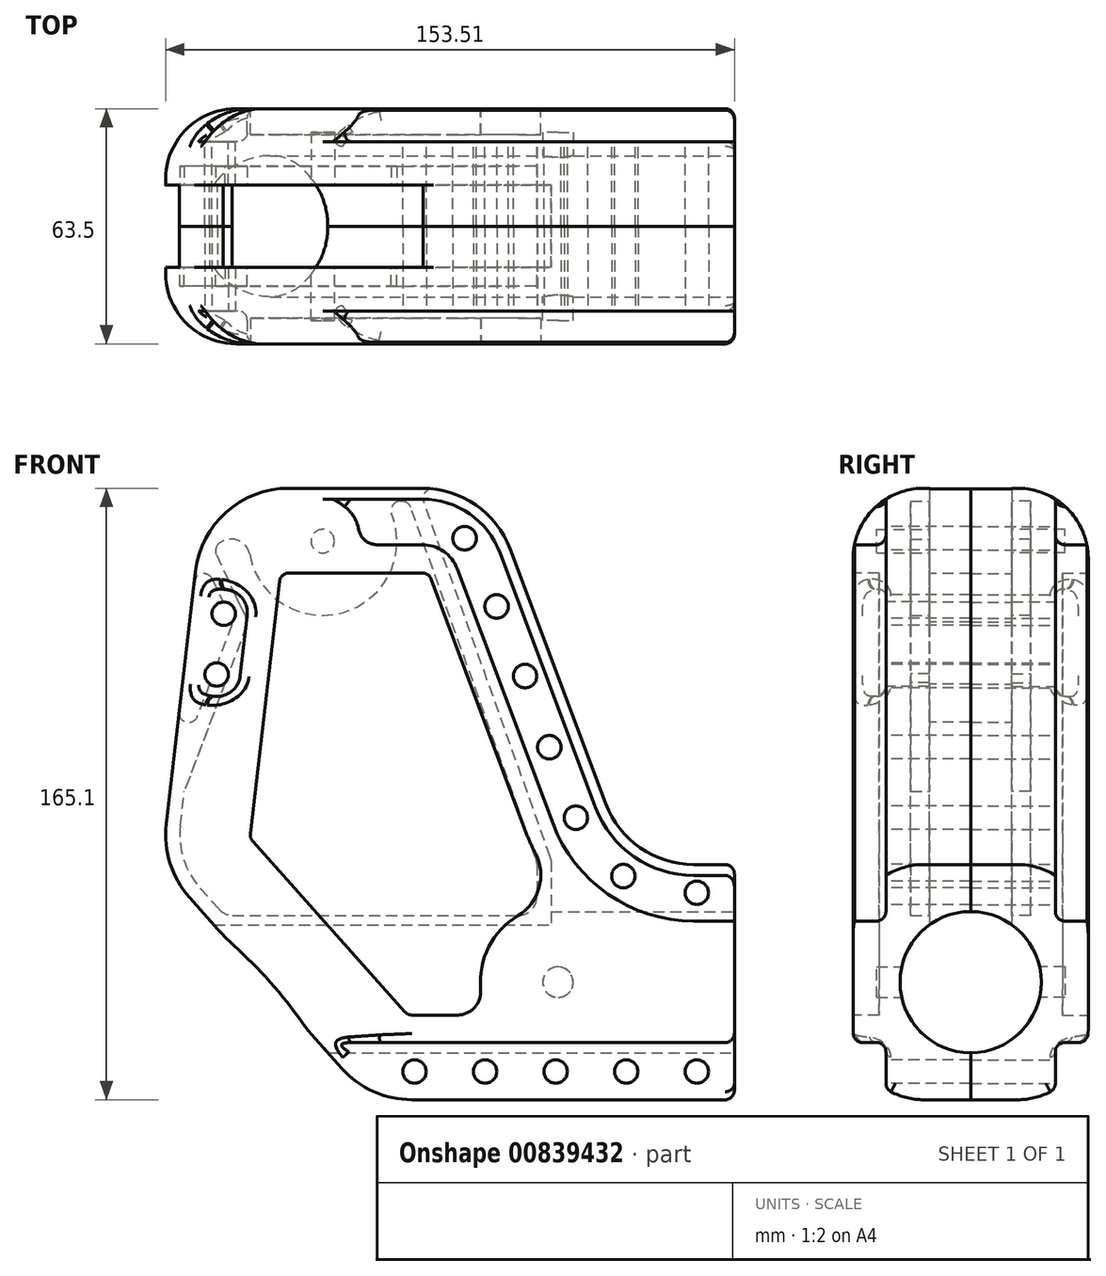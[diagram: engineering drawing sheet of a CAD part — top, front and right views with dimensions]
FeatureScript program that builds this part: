
annotation { "Feature Type Name" : "Feature", "Feature Type Description" : "" }
export const myFeature = defineFeature(function(context is Context, id is Id, definition is map)
    precondition{}
    {
        {
            var Q0;
            Q0=qCreatedBy(makeId("Right.planeOp"),FACE);
            var sketch = newSketch(context, id + "F0", { "sketchPlane" : qUnion([Q0])});
            skCircle(sketch, "E0", {"center": v(0, 0) * mm, "radius": 19.05 * mm});
            skSolve(sketch);
        }
        {
            var Q0;
            Q0=qCreatedBy(makeId("Front.planeOp"),FACE);
            var sketch = newSketch(context, id + "F1", { "sketchPlane" : qUnion([Q0])});
            skCircle(sketch, "E1", {"center": v(0, 0) * mm, "radius": 4.13 * mm});
            skLineSegment(sketch, "E2", {"start": v(0, 0) * mm, "end": v(0, 119.06) * mm, "construction": true});
            skLineSegment(sketch, "E3", {"start": v(0, 119.06) * mm, "end": v(-63.5, 119.06) * mm, "construction": true});
            skCircle(sketch, "E4", {"center": v(-63.5, 119.06) * mm, "radius": 3.18 * mm});
            skLineSegment(sketch, "E5.bottom", {"start": v(-95.25, 133.35) * mm, "end": v(-19.05, 133.35) * mm});
            skLineSegment(sketch, "E5.top", {"start": v(-76.2, -31.75) * mm, "end": v(19.05, -31.75) * mm});
            skLineSegment(sketch, "E5.right", {"start": v(19.05, 31.75) * mm, "end": v(19.05, -31.75) * mm});
            skLineSegment(sketch, "E6", {"start": v(19.05, 31.75) * mm, "end": v(-19.05, 133.35) * mm});
            skPoint(sketch, "E7.orphan", {"position": v(19.05, 133.35) * mm});
            skLineSegment(sketch, "E8", {"start": v(-76.2, -31.75) * mm, "end": v(-114.3, -31.75) * mm});
            skLineSegment(sketch, "E9", {"start": v(-114.3, -31.75) * mm, "end": v(-95.25, 133.35) * mm});
            skLineSegment(sketch, "E10", {"start": v(19.05, 31.75) * mm, "end": v(47.62, 31.75) * mm});
            skLineSegment(sketch, "E11", {"start": v(47.62, 31.75) * mm, "end": v(47.63, -31.75) * mm});
            skLineSegment(sketch, "E12", {"start": v(47.63, -31.75) * mm, "end": v(19.05, -31.75) * mm});
            skLineSegment(sketch, "E13", {"start": v(20.69, 0) * mm, "end": v(20.69, 19.05) * mm, "construction": true});
            skLineSegment(sketch, "E14", {"start": v(20.69, 19.05) * mm, "end": v(20.69, 31.75) * mm, "construction": true});
            skSolve(sketch);
        }
        {
            var Q0;
            Q0 = qSketchRegion(id + "F1", true);
            var Q1;
            Q1=makeQuery(id+"F1.imprint","IMPRINT",FACE,{"disambiguationData":[TD([[makeQuery(id+"F1.imprint","IMPRINT",EDGE,{"derivedFrom":sQuery(id+"F1.wireOp",EDGE,"E1")}),1.0]])]});
            var Q2;
            Q2=makeQuery(id+"F1.imprint","IMPRINT",FACE,{"disambiguationData":[TD([[makeQuery(id+"F1.imprint","IMPRINT",EDGE,{"derivedFrom":sQuery(id+"F1.wireOp",EDGE,"E4")}),1.0]])]});
            extrude(context, id + "F2", {"entities" : qUnion([Q0, Q1, Q2]), "depth" : 63.5 * mm, "offsetDistance" : 25.4 * mm, "symmetric" : true});
        }
        {
            var Q0;
            Q0=makeQuery(id+"F1.imprint","IMPRINT",FACE,{"disambiguationData":[TD([[makeQuery(id+"F1.imprint","IMPRINT",EDGE,{"derivedFrom":sQuery(id+"F1.wireOp",EDGE,"E1")}),1.0]])]});
            extrude(context, id + "F3", {"entities" : qUnion([Q0]), "operationType" : NewBodyOperationType.REMOVE, "depth" : 50.8 * mm, "offsetDistance" : 25.4 * mm, "symmetric" : true});
        }
        {
            var Q0;
            Q0 = qSketchRegion(id + "F0", true);
            extrude(context, id + "F4", {"entities" : qUnion([Q0]), "operationType" : NewBodyOperationType.REMOVE, "endBound" : BoundingType.THROUGH_ALL, "oppositeDirection" : true, "depth" : 25.4 * mm, "offsetDistance" : 25.4 * mm, "hasSecondDirection" : true, "secondDirectionBound" : BoundingType.THROUGH_ALL, "secondDirectionOppositeDirection" : false, "secondDirectionDepth" : 25.4 * mm});
        }
        {
            var Q0;
            Q0=qCreatedBy(makeId("Front.planeOp"),FACE);
            var sketch = newSketch(context, id + "F5", { "sketchPlane" : qUnion([Q0])});
            skLineSegment(sketch, "E15", {"start": v(-1.9, 33.34) * mm, "end": v(-38.1, 134.94) * mm});
            skLineSegment(sketch, "E16", {"start": v(-38.1, 134.94) * mm, "end": v(-105.57, 134.94) * mm});
            skLineSegment(sketch, "E17", {"start": v(-139.7, 33.34) * mm, "end": v(-1.9, 33.34) * mm});
            skLineSegment(sketch, "E18", {"start": v(-1.9, 33.34) * mm, "end": v(-1.9, 0) * mm});
            skLineSegment(sketch, "E19", {"start": v(-1.9, 0) * mm, "end": v(-139.7, 0) * mm});
            skLineSegment(sketch, "E20", {"start": v(-139.7, 0) * mm, "end": v(-139.7, 33.34) * mm});
            skLineSegment(sketch, "E21", {"start": v(-105.57, 134.94) * mm, "end": v(-87.82, 97.04) * mm});
            skLineSegment(sketch, "E22", {"start": v(-87.82, 97.04) * mm, "end": v(-111.76, 33.34) * mm});
            skPoint(sketch, "E23.start.orphan", {"position": v(-139.7, 134.94) * mm});
            skSolve(sketch);
        }
        {
            var Q0;
            Q0 = qSketchRegion(id + "F5", true);
            extrude(context, id + "F6", {"entities" : qUnion([Q0]), "operationType" : NewBodyOperationType.REMOVE, "depth" : 22.22 * mm, "offsetDistance" : 25.4 * mm, "symmetric" : true});
        }
        {
            var Q0;
            Q0=makeQuery(id+"F2.opExtrude","SWEPT_EDGE",EDGE,{"disambiguationData":[OSD([sQuery(id+"F1.wireOp",EDGE,"E8"),sQuery(id+"F1.wireOp",EDGE,"E9")])]});
            chamfer(context, id + "F7", {"entities" : qUnion([Q0]), "width" : 63.5 * mm, "tangentPropagation" : true});
        }
        {
            var Q0;
            Q0=makeQuery(id+"F2.opExtrude","SWEPT_EDGE",EDGE,{"disambiguationData":[OSD([sQuery(id+"F1.wireOp",EDGE,"E5.top"),sQuery(id+"F1.wireOp",EDGE,"E5.right")])]});
            var Q1;
            Q1=makeQuery(id+"F2.opExtrude","SWEPT_EDGE",EDGE,{"disambiguationData":[OSD([sQuery(id+"F1.wireOp",EDGE,"E5.bottom"),sQuery(id+"F1.wireOp",EDGE,"E6")])]});
            var Q2;
            {var subQ0=sQuery(id+"F1.wireOp",EDGE,"E5.bottom");var subQ1=sQuery(id+"F1.wireOp",EDGE,"E9");Q2=makeQuery(id+"F6.boolean.opBoolean","SPLIT",EDGE,{"disambiguationData":[TD([makeQuery(id+"F2.opExtrude","CAP_FACE",FACE,{"disambiguationData":[OSD([subQ0,sQuery(id+"F1.wireOp",EDGE,"E5.top"),sQuery(id+"F1.wireOp",EDGE,"E5.right"),sQuery(id+"F1.wireOp",EDGE,"E6"),sQuery(id+"F1.wireOp",EDGE,"E8"),subQ1])],"isStart":false})])],"derivedFrom":makeQuery(id+"F2.opExtrude","SWEPT_EDGE",EDGE,{"disambiguationData":[OSD([subQ0,subQ1])]})});}
            var Q3;
            {var subQ0=sQuery(id+"F1.wireOp",EDGE,"E5.bottom");var subQ1=sQuery(id+"F1.wireOp",EDGE,"E9");Q3=makeQuery(id+"F6.boolean.opBoolean","SPLIT",EDGE,{"disambiguationData":[TD([makeQuery(id+"F2.opExtrude","CAP_FACE",FACE,{"disambiguationData":[OSD([subQ0,sQuery(id+"F1.wireOp",EDGE,"E5.top"),sQuery(id+"F1.wireOp",EDGE,"E5.right"),sQuery(id+"F1.wireOp",EDGE,"E6"),sQuery(id+"F1.wireOp",EDGE,"E8"),subQ1])],"isStart":true})])],"derivedFrom":makeQuery(id+"F2.opExtrude","SWEPT_EDGE",EDGE,{"disambiguationData":[OSD([subQ0,subQ1])]})});}
            var Q4;
            {var subQ0=sQuery(id+"F1.wireOp",EDGE,"E9");Q4=makeQuery(id+"F7.opChamfer","BLEND_EDGE",EDGE,{"disambiguationData":[OD(1.0)],"blendedFrom":[makeQuery(id+"F2.opExtrude","SWEPT_EDGE",EDGE,{"disambiguationData":[OSD([sQuery(id+"F1.wireOp",EDGE,"E8"),subQ0])]}),makeQuery(id+"F2.opExtrude","SWEPT_FACE",FACE,{"disambiguationData":[OSD([subQ0])]})],"blendedInto":[makeQuery(id+"F2.opExtrude","SWEPT_FACE",FACE,{"disambiguationData":[OSD([subQ0])]})]});}
            var Q5;
            {var subQ0=sQuery(id+"F1.wireOp",EDGE,"E9");Q5=makeQuery(id+"F7.opChamfer","BLEND_EDGE",EDGE,{"disambiguationData":[OD(0.0)],"blendedFrom":[makeQuery(id+"F2.opExtrude","SWEPT_EDGE",EDGE,{"disambiguationData":[OSD([sQuery(id+"F1.wireOp",EDGE,"E8"),subQ0])]}),makeQuery(id+"F2.opExtrude","SWEPT_FACE",FACE,{"disambiguationData":[OSD([subQ0])]})],"blendedInto":[makeQuery(id+"F2.opExtrude","SWEPT_FACE",FACE,{"disambiguationData":[OSD([subQ0])]})]});}
            var Q6;
            {var subQ0=sQuery(id+"F1.wireOp",EDGE,"E8");Q6=makeQuery(id+"F7.opChamfer","BLEND_EDGE",EDGE,{"blendedFrom":[makeQuery(id+"F2.opExtrude","SWEPT_EDGE",EDGE,{"disambiguationData":[OSD([subQ0,sQuery(id+"F1.wireOp",EDGE,"E9")])]}),makeQuery(id+"F2.opExtrude","SWEPT_FACE",FACE,{"disambiguationData":[OSD([sQuery(id+"F1.wireOp",EDGE,"E5.top"),subQ0])]})],"blendedInto":[makeQuery(id+"F2.opExtrude","SWEPT_FACE",FACE,{"disambiguationData":[OSD([sQuery(id+"F1.wireOp",EDGE,"E5.top"),subQ0])]})]});}
            var Q7;
            Q7=makeQuery(id+"F2.opExtrude","SWEPT_EDGE",EDGE,{"disambiguationData":[OSD([sQuery(id+"F1.wireOp",EDGE,"E5.right"),sQuery(id+"F1.wireOp",EDGE,"E6")])]});
            fillet(context, id + "F8", {"entities" : qUnion([Q0, Q1, Q2, Q3, Q4, Q5, Q6, Q7]), "tangentPropagation" : true, "radius" : 25.4 * mm, "defaultsChanged" : false, "vertexSettings" : [], "allowEdgeOverflow" : false});
        }
        {
            var Q0;
            Q0=makeQuery(id+"F1.imprint","IMPRINT",FACE,{"disambiguationData":[TD([[makeQuery(id+"F1.imprint","IMPRINT",EDGE,{"derivedFrom":sQuery(id+"F1.wireOp",EDGE,"E4")}),1.0]])]});
            extrude(context, id + "F9", {"entities" : qUnion([Q0]), "operationType" : NewBodyOperationType.REMOVE, "depth" : 50.8 * mm, "offsetDistance" : 25.4 * mm, "symmetric" : true});
        }
        {
            var Q0;
            Q0=makeQuery(id+"F2.opExtrude","CAP_FACE",FACE,{"disambiguationData":[OSD([sQuery(id+"F1.wireOp",EDGE,"E5.bottom"),sQuery(id+"F1.wireOp",EDGE,"E5.top"),sQuery(id+"F1.wireOp",EDGE,"E5.right"),sQuery(id+"F1.wireOp",EDGE,"E6"),sQuery(id+"F1.wireOp",EDGE,"E8"),sQuery(id+"F1.wireOp",EDGE,"E9")])],"isStart":false});
            var sketch = newSketch(context, id + "F10", { "sketchPlane" : qUnion([Q0])});
            skLineSegment(sketch, "E24", {"start": v(0, 0) * mm, "end": v(108.17, 0) * mm, "construction": true});
            skCircle(sketch, "E25", {"center": v(37.47, -24.13) * mm, "radius": 3.17 * mm});
            skCircle(sketch, "E26.MirrorC", {"center": v(37.47, 24.13) * mm, "radius": 3.17 * mm});
            skCircle(sketch, "E27.1.0.0", {"center": v(18.42, -24.13) * mm, "radius": 3.17 * mm});
            skCircle(sketch, "E27.2.0.0", {"center": v(-0.63, -24.13) * mm, "radius": 3.17 * mm});
            skCircle(sketch, "E27.3.0.0", {"center": v(-19.68, -24.13) * mm, "radius": 3.17 * mm});
            skCircle(sketch, "E27.4.0.0", {"center": v(-38.73, -24.13) * mm, "radius": 3.17 * mm});
            skLineSegment(sketch, "E27.direction1", {"start": v(37.47, -24.13) * mm, "end": v(18.42, -24.13) * mm, "construction": true});
            skCircle(sketch, "E28", {"center": v(17.65, 28.61) * mm, "radius": 3.18 * mm});
            skCircle(sketch, "E29", {"center": v(4.83, 44.38) * mm, "radius": 3.18 * mm});
            skCircle(sketch, "E30", {"center": v(-2.31, 63.4) * mm, "radius": 3.18 * mm});
            skCircle(sketch, "E31", {"center": v(-8.89, 82.63) * mm, "radius": 3.18 * mm});
            skCircle(sketch, "E32", {"center": v(-16.58, 101.44) * mm, "radius": 3.18 * mm});
            skCircle(sketch, "E33", {"center": v(-25.2, 119.84) * mm, "radius": 3.17 * mm});
            skCircle(sketch, "E34", {"center": v(-90.21, 99.46) * mm, "radius": 3.18 * mm});
            skCircle(sketch, "E35", {"center": v(-92.1, 83.06) * mm, "radius": 3.18 * mm});
            skSolve(sketch);
        }
        {
            var Q0;
            Q0 = qSketchRegion(id + "F10", true);
            extrude(context, id + "F11", {"entities" : qUnion([Q0]), "operationType" : NewBodyOperationType.REMOVE, "endBound" : BoundingType.THROUGH_ALL, "oppositeDirection" : true, "depth" : 25.4 * mm, "offsetDistance" : 25.4 * mm});
        }
        {
            var Q0;
            Q0=makeQuery(id+"F2.opExtrude","CAP_EDGE",EDGE,{"disambiguationData":[OSD([sQuery(id+"F1.wireOp",EDGE,"E6")])],"isStart":false});
            var Q1;
            Q1=makeQuery(id+"F2.opExtrude","CAP_EDGE",EDGE,{"disambiguationData":[OSD([sQuery(id+"F1.wireOp",EDGE,"E6")])],"isStart":true});
            fillet(context, id + "F12", {"entities" : qUnion([Q0, Q1]), "tangentPropagation" : true, "radius" : 19.05 * mm, "defaultsChanged" : false, "vertexSettings" : [], "allowEdgeOverflow" : false});
        }
        {
            var Q0;
            Q0=makeQuery(id+"F8.opFillet","BLEND_EDGE",EDGE,{"blendedFrom":[makeQuery(id+"F2.opExtrude","SWEPT_EDGE",EDGE,{"disambiguationData":[OSD([sQuery(id+"F1.wireOp",EDGE,"E5.bottom"),sQuery(id+"F1.wireOp",EDGE,"E6")])]}),makeQuery(id+"F6.boolean.opBoolean","COPY",FACE,{"derivedFrom":makeQuery(id+"F6.opExtrude","SWEPT_FACE",FACE,{"disambiguationData":[OSD([sQuery(id+"F5.wireOp",EDGE,"E15")])]})})],"blendedInto":[makeQuery(id+"F6.boolean.opBoolean","COPY",FACE,{"derivedFrom":makeQuery(id+"F6.opExtrude","SWEPT_FACE",FACE,{"disambiguationData":[OSD([sQuery(id+"F5.wireOp",EDGE,"E15")])]})})]});
            var Q1;
            Q1=makeQuery(id+"F6.boolean.opBoolean","COPY",EDGE,{"derivedFrom":makeQuery(id+"F6.opExtrude","SWEPT_EDGE",EDGE,{"disambiguationData":[OSD([sQuery(id+"F5.wireOp",EDGE,"E15"),sQuery(id+"F5.wireOp",EDGE,"E17"),sQuery(id+"F5.wireOp",EDGE,"E18")])]})});
            fillet(context, id + "F13", {"entities" : qUnion([Q0, Q1]), "tangentPropagation" : true, "radius" : 3.17 * mm, "defaultsChanged" : false, "vertexSettings" : [], "allowEdgeOverflow" : false});
        }
        {
            var Q0;
            Q0=makeQuery(id+"F2.opExtrude","CAP_FACE",FACE,{"disambiguationData":[OSD([sQuery(id+"F1.wireOp",EDGE,"E5.bottom"),sQuery(id+"F1.wireOp",EDGE,"E5.top"),sQuery(id+"F1.wireOp",EDGE,"E5.right"),sQuery(id+"F1.wireOp",EDGE,"E6"),sQuery(id+"F1.wireOp",EDGE,"E8"),sQuery(id+"F1.wireOp",EDGE,"E9")])],"isStart":false});
            var sketch = newSketch(context, id + "F14", { "sketchPlane" : qUnion([Q0])});
            skLineSegment(sketch, "E36.0", {"start": v(-39.41, -8.89) * mm, "end": v(-27.19, -8.89) * mm});
            skLineSegment(sketch, "E36.1", {"start": v(-82.38, 38.04) * mm, "end": v(-41.31, -8.04) * mm});
            skLineSegment(sketch, "E36.2", {"start": v(-75.14, 108.24) * mm, "end": v(-83, 40.02) * mm});
            skLineSegment(sketch, "E36.5", {"start": v(-8.54, 40.2) * mm, "end": v(-34.27, 108.84) * mm});
            skLineSegment(sketch, "E36.6", {"start": v(-36.65, 110.5) * mm, "end": v(-72.61, 110.5) * mm});
            skArc(sketch, "E37.trimOffspring", {"start": v(-10.8, 17.96) * mm, "mid": v(-18.7, 9.46) * mm, "end": v(-20.86, -1.95) * mm});
            skArc(sketch, "E38.trimOffspring", {"start": v(-6.1, 34.74) * mm, "mid": v(-7.4, 37.44) * mm, "end": v(-8.54, 40.2) * mm});
            skPoint(sketch, "E39.visualSharp", {"position": v(-34.9, 110.5) * mm});
            skArc(sketch, "E39.filletArc", {"start": v(-34.27, 108.84) * mm, "mid": v(-35.2, 110.04) * mm, "end": v(-36.65, 110.5) * mm});
            skPoint(sketch, "E40.visualSharp", {"position": v(-74.88, 110.5) * mm});
            skArc(sketch, "E40.filletArc", {"start": v(-72.61, 110.5) * mm, "mid": v(-74.3, 109.85) * mm, "end": v(-75.14, 108.24) * mm});
            skPoint(sketch, "E41.visualSharp", {"position": v(-83.14, 38.9) * mm});
            skArc(sketch, "E41.filletArc", {"start": v(-83, 40.02) * mm, "mid": v(-82.9, 38.96) * mm, "end": v(-82.38, 38.04) * mm});
            skPoint(sketch, "E42.visualSharp", {"position": v(-40.55, -8.89) * mm});
            skArc(sketch, "E42.filletArc", {"start": v(-41.31, -8.04) * mm, "mid": v(-40.45, -8.67) * mm, "end": v(-39.41, -8.89) * mm});
            skPoint(sketch, "E43.visualSharp", {"position": v(-18.98, -8.89) * mm});
            skArc(sketch, "E43.filletArc", {"start": v(-27.19, -8.89) * mm, "mid": v(-22.5, -6.82) * mm, "end": v(-20.86, -1.95) * mm});
            skPoint(sketch, "E44.visualSharp", {"position": v(5.63, 20.19) * mm});
            skArc(sketch, "E44.filletArc", {"start": v(-10.8, 17.96) * mm, "mid": v(-5.1, 25.42) * mm, "end": v(-6.1, 34.74) * mm});
            skPoint(sketch, "E45.visualSharp", {"position": v(16, 13.53) * mm});
            skPoint(sketch, "E46.visualSharp", {"position": v(18.98, -8.89) * mm});
            skArc(sketch, "E47.0", {"start": v(-27.14, 111.52) * mm, "mid": v(-30.87, 116.3) * mm, "end": v(-36.65, 118.11) * mm});
            skLineSegment(sketch, "E47.1", {"start": v(-1.4, 42.88) * mm, "end": v(-27.14, 111.52) * mm});
            skArc(sketch, "E47.2", {"start": v(36.65, 16.51) * mm, "mid": v(13.5, 23.75) * mm, "end": v(-1.4, 42.88) * mm});
            skLineSegment(sketch, "E47.3", {"start": v(47.63, 16.51) * mm, "end": v(36.65, 16.51) * mm});
            skLineSegment(sketch, "E48", {"start": v(-31.55, 138.14) * mm, "end": v(24.8, 112.47) * mm});
            skLineSegment(sketch, "E49", {"start": v(24.8, 112.47) * mm, "end": v(58.9, 66.28) * mm});
            skLineSegment(sketch, "E50", {"start": v(58.9, 66.28) * mm, "end": v(47.62, 16.5) * mm});
            skLineSegment(sketch, "E51.1", {"start": v(-36.65, 118.11) * mm, "end": v(-48.8, 118.11) * mm});
            skArc(sketch, "E52", {"start": v(-53.8, 122.3) * mm, "mid": v(-57.14, 128.06) * mm, "end": v(-63.41, 130.34) * mm});
            skPoint(sketch, "E53.visualSharp", {"position": v(-53.96, 118.11) * mm});
            skArc(sketch, "E53.filletArc", {"start": v(-53.8, 122.3) * mm, "mid": v(-52.06, 119.3) * mm, "end": v(-48.8, 118.11) * mm});
            skLineSegment(sketch, "E54", {"start": v(51.1, -16.3) * mm, "end": v(-82.45, -16.3) * mm});
            skLineSegment(sketch, "E55", {"start": v(-82.45, -16.3) * mm, "end": v(-82.45, -34.82) * mm});
            skLineSegment(sketch, "E56", {"start": v(-82.45, -34.82) * mm, "end": v(52.34, -34.82) * mm});
            skLineSegment(sketch, "E57", {"start": v(52.34, -34.82) * mm, "end": v(51.1, -16.3) * mm});
            skLineSegment(sketch, "E58", {"start": v(-63.41, 130.34) * mm, "end": v(-63.41, 138.14) * mm});
            skLineSegment(sketch, "E59", {"start": v(-63.41, 138.14) * mm, "end": v(-31.55, 138.14) * mm});
            skLineSegment(sketch, "E60.0", {"start": v(-83.88, 98.94) * mm, "end": v(-85.75, 82.73) * mm});
            skLineSegment(sketch, "E61", {"start": v(-89.46, 105.98) * mm, "end": v(-102.52, 107.49) * mm});
            skLineSegment(sketch, "E62", {"start": v(-102.52, 107.49) * mm, "end": v(-105.85, 78.66) * mm});
            skLineSegment(sketch, "E63", {"start": v(-105.85, 78.66) * mm, "end": v(-92.79, 77.15) * mm});
            skPoint(sketch, "E64.visualSharp", {"position": v(-83.15, 105.25) * mm});
            skArc(sketch, "E64.filletArc", {"start": v(-83.88, 98.94) * mm, "mid": v(-85.21, 103.62) * mm, "end": v(-89.46, 105.98) * mm});
            skArc(sketch, "E65.filletArc", {"start": v(-92.79, 77.15) * mm, "mid": v(-88.11, 78.48) * mm, "end": v(-85.75, 82.73) * mm});
            skSolve(sketch);
        }
        {
            var Q0;
            {var subQ1=sQuery(id+"F14.wireOp",EDGE,"E36.3");Q0=makeQuery(id+"F14.imprint","IMPRINT",FACE,{"disambiguationData":[TD([[makeQuery(id+"F14.imprint","IMPRINT",EDGE,{"derivedFrom":subQ1}),1.0]])]});}
            var Q1;
            Q1=makeQuery(id+"F14.imprint","IMPRINT",FACE,{"disambiguationData":[TD([[makeQuery(id+"F14.imprint","IMPRINT",EDGE,{"derivedFrom":sQuery(id+"F14.wireOp",EDGE,"E36.0")}),1.0]])]});
            extrude(context, id + "F15", {"entities" : qUnion([Q0, Q1]), "operationType" : NewBodyOperationType.REMOVE, "oppositeDirection" : true, "depth" : 7 * mm, "offsetDistance" : 25.4 * mm});
        }
        {
            var Q0;
            Q0=makeQuery(id+"F12.opFillet","BLEND_EDGE",EDGE,{"blendedFrom":[makeQuery(id+"F2.opExtrude","CAP_EDGE",EDGE,{"disambiguationData":[OSD([sQuery(id+"F1.wireOp",EDGE,"E10")])],"isStart":false}),makeQuery(id+"F2.opExtrude","SWEPT_FACE",FACE,{"disambiguationData":[OSD([sQuery(id+"F1.wireOp",EDGE,"E11")])]})],"blendedInto":[makeQuery(id+"F2.opExtrude","SWEPT_FACE",FACE,{"disambiguationData":[OSD([sQuery(id+"F1.wireOp",EDGE,"E11")])]})]});
            fillet(context, id + "F16", {"entities" : qUnion([Q0]), "tangentPropagation" : true, "radius" : 2.54 * mm, "defaultsChanged" : true, "vertexSettings" : [], "allowEdgeOverflow" : false});
        }
        {
            var Q0;
            Q0=makeQuery(id+"F14.imprint","IMPRINT",FACE,{"disambiguationData":[TD([[makeQuery(id+"F14.imprint","IMPRINT",EDGE,{"derivedFrom":sQuery(id+"F14.wireOp",EDGE,"E47.0")}),-1.0]])]});
            var Q1;
            Q1=makeQuery(id+"F14.imprint","IMPRINT",FACE,{"disambiguationData":[TD([[makeQuery(id+"F14.imprint","IMPRINT",EDGE,{"derivedFrom":sQuery(id+"F14.wireOp",EDGE,"E54")}),1.0]])]});
            var Q2;
            Q2=makeQuery(id+"F14.imprint","IMPRINT",FACE,{"disambiguationData":[TD([[makeQuery(id+"F14.imprint","IMPRINT",EDGE,{"derivedFrom":sQuery(id+"F14.wireOp",EDGE,"E60.0")}),-1.0]])]});
            extrude(context, id + "F17", {"entities" : qUnion([Q0, Q1, Q2]), "operationType" : NewBodyOperationType.REMOVE, "oppositeDirection" : true, "depth" : 8.9 * mm, "offsetDistance" : 25.4 * mm});
        }
        {
            var Q0;
            Q0=makeQuery(id+"F17.boolean.opBoolean","COPY",EDGE,{"derivedFrom":makeQuery(id+"F17.opExtrude","CAP_EDGE",EDGE,{"disambiguationData":[OSD([sQuery(id+"F14.wireOp",EDGE,"E47.1")])],"isStart":false})});
            var Q1;
            Q1=makeQuery(id+"F17.boolean.opBoolean","COPY",EDGE,{"derivedFrom":makeQuery(id+"F17.opExtrude","CAP_EDGE",EDGE,{"disambiguationData":[OSD([sQuery(id+"F14.wireOp",EDGE,"E54")])],"isStart":false})});
            var Q2;
            Q2=makeQuery(id+"F17.boolean.opBoolean","COPY",EDGE,{"derivedFrom":makeQuery(id+"F17.opExtrude","CAP_EDGE",EDGE,{"disambiguationData":[OSD([sQuery(id+"F14.wireOp",EDGE,"E60.0")])],"isStart":false})});
            fillet(context, id + "F18", {"entities" : qUnion([Q0, Q1, Q2]), "tangentPropagation" : true, "radius" : 2.54 * mm, "defaultsChanged" : false, "vertexSettings" : [], "allowEdgeOverflow" : false});
        }
        {
            var Q0;
            {var subQ0=sQuery(id+"F1.wireOp",EDGE,"E12");var subQ1=sQuery(id+"F1.wireOp",EDGE,"E8");var subQ2=sQuery(id+"F1.wireOp",EDGE,"E5.top");Q0=makeQuery(id+"F17.boolean.opBoolean","INTERSECT",EDGE,{"derivedFrom":[makeQuery(id+"F12.opFillet","BLEND_FACE",FACE,{"disambiguationData":[OSD([subQ2,subQ1,subQ0]),TDD([makeQuery(id+"F2.opExtrude","CAP_EDGE",EDGE,{"disambiguationData":[OSD([subQ2,subQ1,subQ0])],"isStart":false})])]}),makeQuery(id+"F17.opExtrude","SWEPT_FACE",FACE,{"disambiguationData":[OSD([sQuery(id+"F14.wireOp",EDGE,"E54")])]})]});}
            var Q1;
            {var subQ0=sQuery(id+"F1.wireOp",EDGE,"E12");var subQ1=sQuery(id+"F1.wireOp",EDGE,"E8");var subQ2=sQuery(id+"F1.wireOp",EDGE,"E5.top");Q1=makeQuery(id+"F17.boolean.opBoolean","INTERSECT",EDGE,{"derivedFrom":[makeQuery(id+"F12.opFillet","BLEND_FACE",FACE,{"disambiguationData":[OSD([subQ2,subQ1,subQ0]),TDD([makeQuery(id+"F2.opExtrude","CAP_EDGE",EDGE,{"disambiguationData":[OSD([subQ2,subQ1,subQ0])],"isStart":false})])]}),makeQuery(id+"F17.opExtrude","CAP_FACE",FACE,{"disambiguationData":[OSD([sQuery(id+"F14.wireOp",EDGE,"E54"),sQuery(id+"F14.wireOp",EDGE,"E55"),sQuery(id+"F14.wireOp",EDGE,"E56"),sQuery(id+"F14.wireOp",EDGE,"E57")])],"isStart":false})]});}
            var Q2;
            {var subQ0=sQuery(id+"F1.wireOp",EDGE,"E12");var subQ1=sQuery(id+"F1.wireOp",EDGE,"E11");var subQ2=sQuery(id+"F1.wireOp",EDGE,"E10");var subQ3=sQuery(id+"F1.wireOp",EDGE,"E9");var subQ4=sQuery(id+"F1.wireOp",EDGE,"E8");var subQ5=sQuery(id+"F1.wireOp",EDGE,"E6");var subQ6=sQuery(id+"F1.wireOp",EDGE,"E5.top");var subQ7=sQuery(id+"F1.wireOp",EDGE,"E5.bottom");var subQ8=sQuery(id+"F1.wireOp",EDGE,"E5.right");Q2=makeQuery(id+"F17.boolean.opBoolean","INTERSECT",EDGE,{"derivedFrom":[makeQuery(id+"F12.opFillet","BLEND_FACE",FACE,{"disambiguationData":[OSD([subQ7,subQ6,subQ8,subQ5,subQ4,subQ3,subQ2,subQ1,subQ0]),TDD([makeQuery(id+"F8.opFillet","BLEND_EDGE",EDGE,{"blendedFrom":[makeQuery(id+"F2.opExtrude","SWEPT_EDGE",EDGE,{"disambiguationData":[OSD([subQ8,subQ5,subQ2])]}),makeQuery(id+"F2.opExtrude","CAP_FACE",FACE,{"disambiguationData":[OSD([subQ7,subQ6,subQ5,subQ4,subQ3,subQ2,subQ1,subQ0])],"isStart":false})],"blendedInto":[makeQuery(id+"F2.opExtrude","CAP_FACE",FACE,{"disambiguationData":[OSD([subQ7,subQ6,subQ5,subQ4,subQ3,subQ2,subQ1,subQ0])],"isStart":false})]})])]}),makeQuery(id+"F17.opExtrude","SWEPT_FACE",FACE,{"disambiguationData":[OSD([sQuery(id+"F14.wireOp",EDGE,"E47.2")])]})]});}
            var Q3;
            Q3=makeQuery(id+"F15.boolean.opBoolean","COPY",EDGE,{"derivedFrom":makeQuery(id+"F15.opExtrude","CAP_EDGE",EDGE,{"disambiguationData":[OSD([sQuery(id+"F14.wireOp",EDGE,"E36.5")])],"isStart":true})});
            var Q4;
            {var subQ0=sQuery(id+"F1.wireOp",EDGE,"E9");Q4=makeQuery(id+"F17.boolean.opBoolean","INTERSECT",EDGE,{"derivedFrom":[makeQuery(id+"F12.opFillet","BLEND_FACE",FACE,{"disambiguationData":[OSD([subQ0]),TDD([makeQuery(id+"F2.opExtrude","CAP_EDGE",EDGE,{"disambiguationData":[OSD([subQ0])],"isStart":false})])]}),makeQuery(id+"F17.opExtrude","SWEPT_FACE",FACE,{"disambiguationData":[OSD([sQuery(id+"F14.wireOp",EDGE,"E60.0")])]})]});}
            fillet(context, id + "F19", {"entities" : qUnion([Q0, Q1, Q2, Q3, Q4]), "tangentPropagation" : true, "radius" : 2.54 * mm, "defaultsChanged" : false, "vertexSettings" : [], "allowEdgeOverflow" : false});
        }
        {
            var Q0;
            Q0=qCreatedBy(makeId("Front.planeOp"),FACE);
            var sketch = newSketch(context, id + "F20", { "sketchPlane" : qUnion([Q0])});
            skLineSegment(sketch, "E66.bottom", {"start": v(-108.56, -43.65) * mm, "end": v(63.43, -43.65) * mm});
            skLineSegment(sketch, "E66.top", {"start": v(-108.56, 138.76) * mm, "end": v(63.43, 138.76) * mm});
            skLineSegment(sketch, "E66.left", {"start": v(-108.56, -43.65) * mm, "end": v(-108.56, 138.76) * mm});
            skLineSegment(sketch, "E66.right", {"start": v(63.43, -43.65) * mm, "end": v(63.43, 138.76) * mm});
            skSolve(sketch);
        }
        {
            var Q0;
            Q0 = qSketchRegion(id + "F20", true);
            extrude(context, id + "F21", {"entities" : qUnion([Q0]), "operationType" : NewBodyOperationType.REMOVE, "endBound" : BoundingType.THROUGH_ALL, "oppositeDirection" : true, "depth" : 25.4 * mm, "offsetDistance" : 25.4 * mm});
        }
        {
            var Q0;
            Q0=makeQuery(id+"F6.boolean.opBoolean","COPY",FACE,{"derivedFrom":makeQuery(id+"F6.opExtrude","CAP_FACE",FACE,{"disambiguationData":[OSD([sQuery(id+"F5.wireOp",EDGE,"E15"),sQuery(id+"F5.wireOp",EDGE,"E16"),sQuery(id+"F5.wireOp",EDGE,"E23"),sQuery(id+"F5.wireOp",EDGE,"E18"),sQuery(id+"F5.wireOp",EDGE,"E19"),sQuery(id+"F5.wireOp",EDGE,"E20")])],"isStart":false})});
            var sketch = newSketch(context, id + "F22", { "sketchPlane" : qUnion([Q0])});
            skArc(sketch, "E67", {"start": v(44.87, 126.4) * mm, "mid": v(58.01, 99.81) * mm, "end": v(83.2, 115.47) * mm});
            skArc(sketch, "E68.1", {"start": v(96.6, 25.37) * mm, "mid": v(101.07, 33.22) * mm, "end": v(101.93, 42.2) * mm});
            skLineSegment(sketch, "E68.3", {"start": v(91.56, 19.7) * mm, "end": v(96.6, 25.37) * mm});
            skLineSegment(sketch, "E68.4", {"start": v(42.51, 129.86) * mm, "end": v(42.13, 129.86) * mm});
            skLineSegment(sketch, "E68.5", {"start": v(6, 33.5) * mm, "end": v(39.74, 128.18) * mm});
            skLineSegment(sketch, "E68.6", {"start": v(5.7, 31.8) * mm, "end": v(5.7, 23.09) * mm});
            skLineSegment(sketch, "E68.7", {"start": v(87.77, 18) * mm, "end": v(10.78, 18) * mm});
            skPoint(sketch, "E69.visualSharp", {"position": v(81.3, 128.22) * mm});
            skArc(sketch, "E69.filletArc", {"start": v(91.6, 118.32) * mm, "mid": v(86.56, 119.37) * mm, "end": v(83.2, 115.47) * mm});
            skPoint(sketch, "E70.visualSharp", {"position": v(46.65, 129.86) * mm});
            skArc(sketch, "E70.filletArc", {"start": v(44.87, 126.4) * mm, "mid": v(44.61, 128.75) * mm, "end": v(42.51, 129.86) * mm});
            skPoint(sketch, "E71.visualSharp", {"position": v(40.34, 129.86) * mm});
            skArc(sketch, "E71.filletArc", {"start": v(42.13, 129.86) * mm, "mid": v(40.66, 129.4) * mm, "end": v(39.74, 128.18) * mm});
            skPoint(sketch, "E72.visualSharp", {"position": v(5.7, 32.68) * mm});
            skArc(sketch, "E72.filletArc", {"start": v(6, 33.5) * mm, "mid": v(5.77, 32.67) * mm, "end": v(5.7, 31.8) * mm});
            skPoint(sketch, "E73.visualSharp", {"position": v(5.7, 18) * mm});
            skArc(sketch, "E73.filletArc", {"start": v(5.7, 23.09) * mm, "mid": v(7.19, 19.5) * mm, "end": v(10.78, 18) * mm});
            skPoint(sketch, "E74.visualSharp", {"position": v(90.04, 18) * mm});
            skArc(sketch, "E74.filletArc", {"start": v(87.77, 18) * mm, "mid": v(89.84, 18.45) * mm, "end": v(91.56, 19.7) * mm});
            skLineSegment(sketch, "E75.0", {"start": v(101.93, 42.2) * mm, "end": v(100.86, 51.52) * mm});
            skLineSegment(sketch, "E75.1", {"start": v(84.07, 96.2) * mm, "end": v(100.86, 51.52) * mm});
            skLineSegment(sketch, "E75.2", {"start": v(92.2, 115.36) * mm, "end": v(84.14, 98.18) * mm});
            skPoint(sketch, "E76.visualSharp", {"position": v(83.7, 97.2) * mm});
            skArc(sketch, "E76.filletArc", {"start": v(84.14, 98.18) * mm, "mid": v(83.9, 97.2) * mm, "end": v(84.07, 96.2) * mm});
            skPoint(sketch, "E77.visualSharp", {"position": v(92.8, 116.67) * mm});
            skArc(sketch, "E77.filletArc", {"start": v(92.2, 115.36) * mm, "mid": v(92.38, 116.94) * mm, "end": v(91.6, 118.32) * mm});
            skSolve(sketch);
        }
        {
            var Q0;
            Q0 = qSketchRegion(id + "F22", true);
            extrude(context, id + "F23", {"entities" : qUnion([Q0]), "operationType" : NewBodyOperationType.REMOVE, "oppositeDirection" : true, "depth" : 5.08 * mm, "offsetDistance" : 25.4 * mm});
        }
        {
            var Q0;
            {var subQ0=sQuery(id+"F5.wireOp",EDGE,"E21");var subQ1=sQuery(id+"F1.wireOp",EDGE,"E5.bottom");var subQ2=sQuery(id+"F1.wireOp",EDGE,"E9");Q0=makeQuery(id+"F25.opPattern","COPY",EDGE,{"derivedFrom":makeQuery(id+"F8.opFillet","BLEND_EDGE",EDGE,{"blendedFrom":[makeQuery(id+"F6.boolean.opBoolean","SPLIT",EDGE,{"disambiguationData":[TD([makeQuery(id+"F2.opExtrude","CAP_FACE",FACE,{"disambiguationData":[OSD([subQ1,sQuery(id+"F1.wireOp",EDGE,"E5.top"),sQuery(id+"F1.wireOp",EDGE,"E6"),sQuery(id+"F1.wireOp",EDGE,"E8"),subQ2,sQuery(id+"F1.wireOp",EDGE,"E10"),sQuery(id+"F1.wireOp",EDGE,"E11"),sQuery(id+"F1.wireOp",EDGE,"E12")])],"isStart":false})])],"derivedFrom":makeQuery(id+"F2.opExtrude","SWEPT_EDGE",EDGE,{"disambiguationData":[OSD([subQ1,subQ2])]})}),makeQuery(id+"F6.boolean.opBoolean","COPY",FACE,{"derivedFrom":makeQuery(id+"F6.opExtrude","SWEPT_FACE",FACE,{"disambiguationData":[OSD([subQ0])]})})],"blendedInto":[makeQuery(id+"F6.boolean.opBoolean","COPY",FACE,{"derivedFrom":makeQuery(id+"F6.opExtrude","SWEPT_FACE",FACE,{"disambiguationData":[OSD([subQ0])]})})]}),"instanceName":"1"});}
            var Q1;
            {var subQ0=sQuery(id+"F5.wireOp",EDGE,"E21");var subQ1=sQuery(id+"F1.wireOp",EDGE,"E5.bottom");var subQ2=sQuery(id+"F1.wireOp",EDGE,"E9");Q1=makeQuery(id+"F8.opFillet","BLEND_EDGE",EDGE,{"blendedFrom":[makeQuery(id+"F6.boolean.opBoolean","SPLIT",EDGE,{"disambiguationData":[TD([makeQuery(id+"F2.opExtrude","CAP_FACE",FACE,{"disambiguationData":[OSD([subQ1,sQuery(id+"F1.wireOp",EDGE,"E5.top"),sQuery(id+"F1.wireOp",EDGE,"E6"),sQuery(id+"F1.wireOp",EDGE,"E8"),subQ2,sQuery(id+"F1.wireOp",EDGE,"E10"),sQuery(id+"F1.wireOp",EDGE,"E11"),sQuery(id+"F1.wireOp",EDGE,"E12")])],"isStart":false})])],"derivedFrom":makeQuery(id+"F2.opExtrude","SWEPT_EDGE",EDGE,{"disambiguationData":[OSD([subQ1,subQ2])]})}),makeQuery(id+"F6.boolean.opBoolean","COPY",FACE,{"derivedFrom":makeQuery(id+"F6.opExtrude","SWEPT_FACE",FACE,{"disambiguationData":[OSD([subQ0])]})})],"blendedInto":[makeQuery(id+"F6.boolean.opBoolean","COPY",FACE,{"derivedFrom":makeQuery(id+"F6.opExtrude","SWEPT_FACE",FACE,{"disambiguationData":[OSD([subQ0])]})})]});}
            var Q2;
            Q2=makeQuery(id+"F25.opPattern","COPY",EDGE,{"derivedFrom":makeQuery(id+"F6.boolean.opBoolean","INTERSECT",EDGE,{"derivedFrom":[makeQuery(id+"F2.opExtrude","SWEPT_FACE",FACE,{"disambiguationData":[OSD([sQuery(id+"F1.wireOp",EDGE,"E9")])]}),makeQuery(id+"F6.opExtrude","SWEPT_FACE",FACE,{"disambiguationData":[OSD([sQuery(id+"F5.wireOp",EDGE,"E22")])]})]}),"instanceName":"1"});
            var Q3;
            Q3=makeQuery(id+"F6.boolean.opBoolean","INTERSECT",EDGE,{"derivedFrom":[makeQuery(id+"F2.opExtrude","SWEPT_FACE",FACE,{"disambiguationData":[OSD([sQuery(id+"F1.wireOp",EDGE,"E9")])]}),makeQuery(id+"F6.opExtrude","SWEPT_FACE",FACE,{"disambiguationData":[OSD([sQuery(id+"F5.wireOp",EDGE,"E22")])]})]});
            var Q4;
            Q4=makeQuery(id+"F6.boolean.opBoolean","COPY",EDGE,{"derivedFrom":makeQuery(id+"F6.opExtrude","SWEPT_EDGE",EDGE,{"disambiguationData":[OSD([sQuery(id+"F5.wireOp",EDGE,"E21"),sQuery(id+"F5.wireOp",EDGE,"E22")])]})});
            var Q5;
            Q5=makeQuery(id+"F25.opPattern","COPY",EDGE,{"derivedFrom":makeQuery(id+"F6.boolean.opBoolean","COPY",EDGE,{"derivedFrom":makeQuery(id+"F6.opExtrude","SWEPT_EDGE",EDGE,{"disambiguationData":[OSD([sQuery(id+"F5.wireOp",EDGE,"E21"),sQuery(id+"F5.wireOp",EDGE,"E22")])]})}),"instanceName":"1"});
            var Q6;
            Q6=makeQuery(id+"F6.boolean.opBoolean","INTERSECT",EDGE,{"derivedFrom":[makeQuery(id+"F2.opExtrude","SWEPT_FACE",FACE,{"disambiguationData":[OSD([sQuery(id+"F1.wireOp",EDGE,"E5.bottom")])]}),makeQuery(id+"F6.opExtrude","SWEPT_FACE",FACE,{"disambiguationData":[OSD([sQuery(id+"F5.wireOp",EDGE,"E15")])]})]});
            fillet(context, id + "F24", {"entities" : qUnion([Q0, Q1, Q2, Q3, Q4, Q5, Q6]), "tangentPropagation" : true, "radius" : 2.54 * mm, "defaultsChanged" : false, "vertexSettings" : [], "allowEdgeOverflow" : false});
        }
        {
            var Q0;
            Q0=makeQuery(id+"F2.opExtrude","SWEPT_BODY",BODY,{"disambiguationData":[OSD([sQuery(id+"F1.wireOp",EDGE,"E5.bottom"),sQuery(id+"F1.wireOp",EDGE,"E5.top"),sQuery(id+"F1.wireOp",EDGE,"E6"),sQuery(id+"F1.wireOp",EDGE,"E8"),sQuery(id+"F1.wireOp",EDGE,"E9"),sQuery(id+"F1.wireOp",EDGE,"E10"),sQuery(id+"F1.wireOp",EDGE,"E11"),sQuery(id+"F1.wireOp",EDGE,"E12")])]});
            var Q1;
            Q1=qCreatedBy(makeId("Front.planeOp"),FACE);
            mirror(context, id + "F25", {"entities" : qUnion([Q0]), "mirrorPlane" : qUnion([Q1])});
        }
    });
